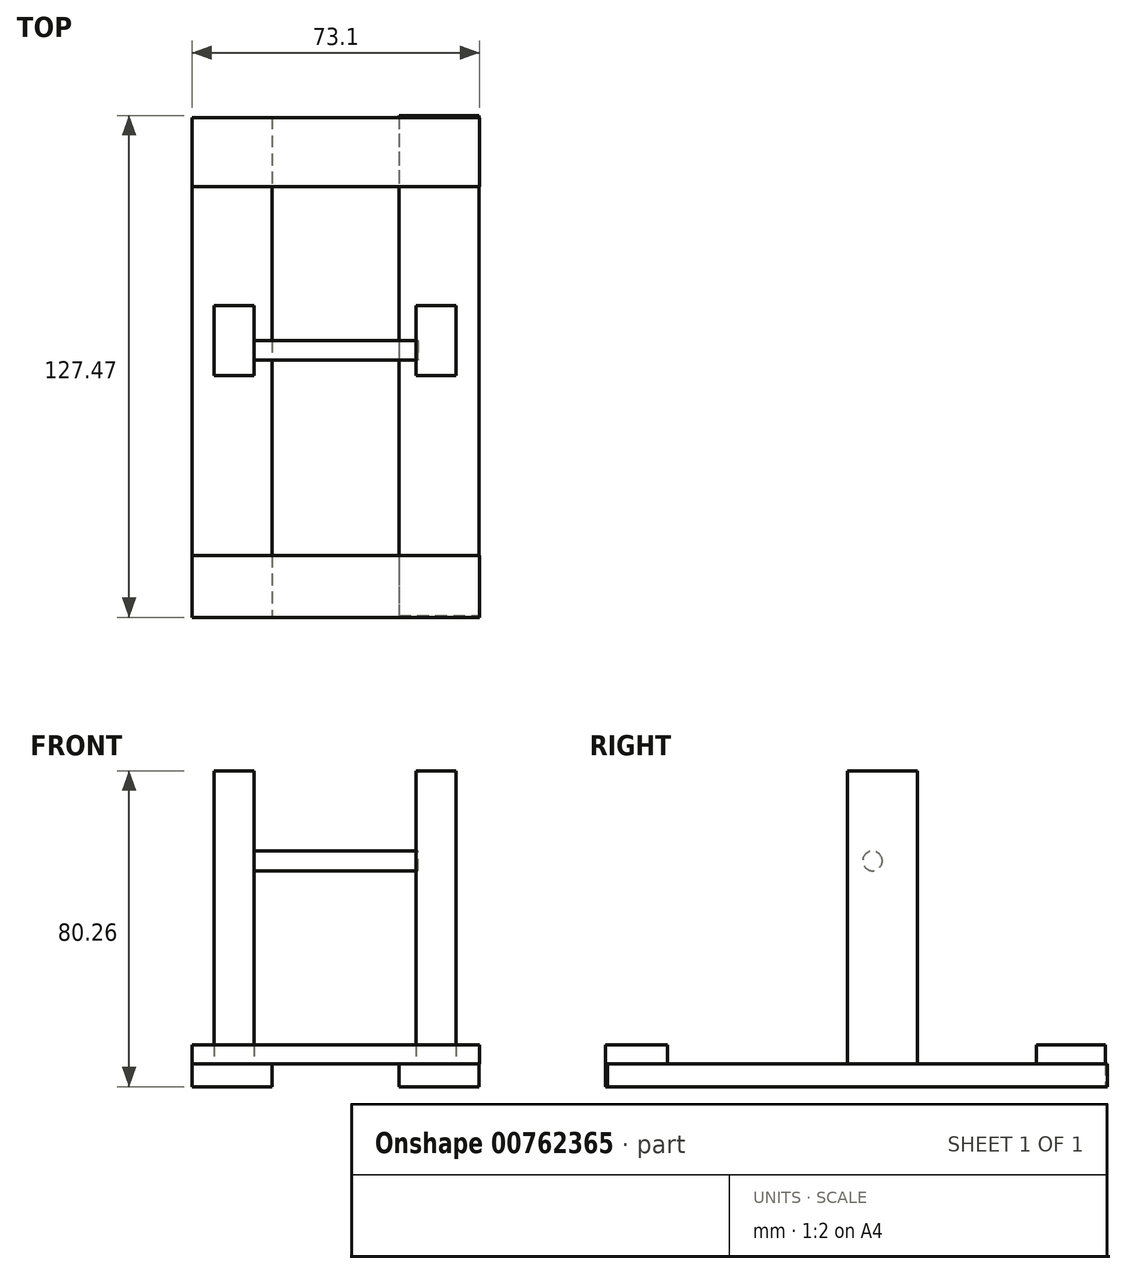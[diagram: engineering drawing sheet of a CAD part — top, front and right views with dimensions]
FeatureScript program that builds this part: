
annotation { "Feature Type Name" : "Feature", "Feature Type Description" : "" }
export const myFeature = defineFeature(function(context is Context, id is Id, definition is map)
    precondition{}
    {
        {
            var Q0;
            Q0=qCreatedBy(makeId("Top.planeOp"),FACE);
            var sketch = newSketch(context, id + "F0", { "sketchPlane" : qUnion([Q0])});
            skLineSegment(sketch, "E0.bottom", {"start": v(-47.27, 47.75) * mm, "end": v(-26.95, 47.75) * mm});
            skLineSegment(sketch, "E0.top", {"start": v(-47.27, -79.25) * mm, "end": v(-26.95, -79.25) * mm});
            skLineSegment(sketch, "E0.left", {"start": v(-47.27, 47.75) * mm, "end": v(-47.27, -79.25) * mm});
            skLineSegment(sketch, "E0.right", {"start": v(-26.95, 47.75) * mm, "end": v(-26.95, -79.25) * mm});
            skLineSegment(sketch, "E1.bottom", {"start": v(5.32, 48.22) * mm, "end": v(25.64, 48.22) * mm});
            skLineSegment(sketch, "E1.top", {"start": v(5.32, -78.78) * mm, "end": v(25.64, -78.78) * mm});
            skLineSegment(sketch, "E1.left", {"start": v(5.32, 48.22) * mm, "end": v(5.32, -78.78) * mm});
            skLineSegment(sketch, "E1.right", {"start": v(25.64, 48.22) * mm, "end": v(25.64, -78.78) * mm});
            skSolve(sketch);
        }
        {
            var Q0;
            Q0=makeQuery(id+"F0.imprint","IMPRINT",FACE,{"disambiguationData":[TD([[makeQuery(id+"F0.imprint","IMPRINT",EDGE,{"derivedFrom":sQuery(id+"F0.wireOp",EDGE,"E0.bottom")}),-1.0]])]});
            var Q1;
            Q1=makeQuery(id+"F0.imprint","IMPRINT",FACE,{"disambiguationData":[TD([[makeQuery(id+"F0.imprint","IMPRINT",EDGE,{"derivedFrom":sQuery(id+"F0.wireOp",EDGE,"E1.bottom")}),-1.0]])]});
            extrude(context, id + "F1", {"entities" : qUnion([Q0, Q1]), "depth" : 5.84 * mm, "offsetDistance" : 25.4 * mm});
        }
        {
            var Q0;
            Q0=makeQuery(id+"F1.opExtrude","CAP_FACE",FACE,{"disambiguationData":[OSD([sQuery(id+"F0.wireOp",EDGE,"E0.bottom"),sQuery(id+"F0.wireOp",EDGE,"E0.top"),sQuery(id+"F0.wireOp",EDGE,"E0.left"),sQuery(id+"F0.wireOp",EDGE,"E0.right")])],"isStart":false});
            var sketch = newSketch(context, id + "F2", { "sketchPlane" : qUnion([Q0])});
            skLineSegment(sketch, "E2.bottom", {"start": v(-41.67, 0) * mm, "end": v(-31.51, 0) * mm});
            skLineSegment(sketch, "E2.top", {"start": v(-41.67, -17.78) * mm, "end": v(-31.51, -17.78) * mm});
            skLineSegment(sketch, "E2.left", {"start": v(-41.67, 0) * mm, "end": v(-41.67, -17.78) * mm});
            skLineSegment(sketch, "E2.right", {"start": v(-31.51, 0) * mm, "end": v(-31.51, -17.78) * mm});
            skLineSegment(sketch, "E3.bottom", {"start": v(9.68, 0) * mm, "end": v(19.84, 0) * mm});
            skLineSegment(sketch, "E3.top", {"start": v(9.68, -17.78) * mm, "end": v(19.84, -17.78) * mm});
            skLineSegment(sketch, "E3.left", {"start": v(9.68, 0) * mm, "end": v(9.68, -17.78) * mm});
            skLineSegment(sketch, "E3.right", {"start": v(19.84, 0) * mm, "end": v(19.84, -17.78) * mm});
            skSolve(sketch);
        }
        {
            var Q0;
            Q0=makeQuery(id+"F2.imprint","IMPRINT",FACE,{"disambiguationData":[TD([[makeQuery(id+"F2.imprint","IMPRINT",EDGE,{"derivedFrom":sQuery(id+"F2.wireOp",EDGE,"E2.bottom")}),-1.0]])]});
            var Q1;
            Q1=makeQuery(id+"F2.imprint","IMPRINT",FACE,{"disambiguationData":[TD([[makeQuery(id+"F2.imprint","IMPRINT",EDGE,{"derivedFrom":sQuery(id+"F2.wireOp",EDGE,"E3.bottom")}),-1.0]])]});
            extrude(context, id + "F3", {"entities" : qUnion([Q0, Q1]), "depth" : 74.42 * mm, "offsetDistance" : 25.4 * mm});
        }
        {
            var Q0;
            Q0=makeQuery(id+"F3.opExtrude","SWEPT_FACE",FACE,{"disambiguationData":[OSD([sQuery(id+"F2.wireOp",EDGE,"E2.left")])]});
            var sketch = newSketch(context, id + "F4", { "sketchPlane" : qUnion([Q0])});
            skLineSegment(sketch, "E4", {"start": v(8.89, 80.26) * mm, "end": v(8.89, 5.84) * mm});
            skSolve(sketch);
        }
        {
            var Q0;
            Q0=makeQuery(id+"F3.opExtrude","SWEPT_FACE",FACE,{"disambiguationData":[OSD([sQuery(id+"F2.wireOp",EDGE,"E2.right")])]});
            var sketch = newSketch(context, id + "F5", { "sketchPlane" : qUnion([Q0])});
            skCircle(sketch, "E5", {"center": v(-11.47, 57.35) * mm, "radius": 2.49 * mm});
            skSolve(sketch);
        }
        {
            var Q0;
            Q0 = qSketchRegion(id + "F5", true);
            extrude(context, id + "F6", {"entities" : qUnion([Q0]), "depth" : 41.66 * mm, "offsetDistance" : 25.4 * mm});
        }
        {
            var Q0;
            Q0=makeQuery(id+"F1.opExtrude","CAP_FACE",FACE,{"disambiguationData":[OSD([sQuery(id+"F0.wireOp",EDGE,"E0.bottom"),sQuery(id+"F0.wireOp",EDGE,"E0.top"),sQuery(id+"F0.wireOp",EDGE,"E0.left"),sQuery(id+"F0.wireOp",EDGE,"E0.right")])],"isStart":false});
            var sketch = newSketch(context, id + "F7", { "sketchPlane" : qUnion([Q0])});
            skLineSegment(sketch, "E6.bottom", {"start": v(-47.27, -79.25) * mm, "end": v(25.83, -79.25) * mm});
            skLineSegment(sketch, "E6.top", {"start": v(-47.27, -63.56) * mm, "end": v(25.83, -63.56) * mm});
            skLineSegment(sketch, "E6.left", {"start": v(-47.27, -79.25) * mm, "end": v(-47.27, -63.56) * mm});
            skLineSegment(sketch, "E6.right", {"start": v(25.83, -79.25) * mm, "end": v(25.83, -63.56) * mm});
            skLineSegment(sketch, "E7.bottom", {"start": v(-47.27, 47.75) * mm, "end": v(25.83, 47.75) * mm});
            skLineSegment(sketch, "E7.top", {"start": v(-47.27, 30.23) * mm, "end": v(25.83, 30.23) * mm});
            skLineSegment(sketch, "E7.left", {"start": v(-47.27, 47.75) * mm, "end": v(-47.27, 30.23) * mm});
            skLineSegment(sketch, "E7.right", {"start": v(25.83, 47.75) * mm, "end": v(25.83, 30.23) * mm});
            skSolve(sketch);
        }
        {
            var Q0;
            Q0 = qSketchRegion(id + "F7", true);
            extrude(context, id + "F8", {"entities" : qUnion([Q0]), "depth" : 4.83 * mm, "offsetDistance" : 25.4 * mm});
        }
    });
